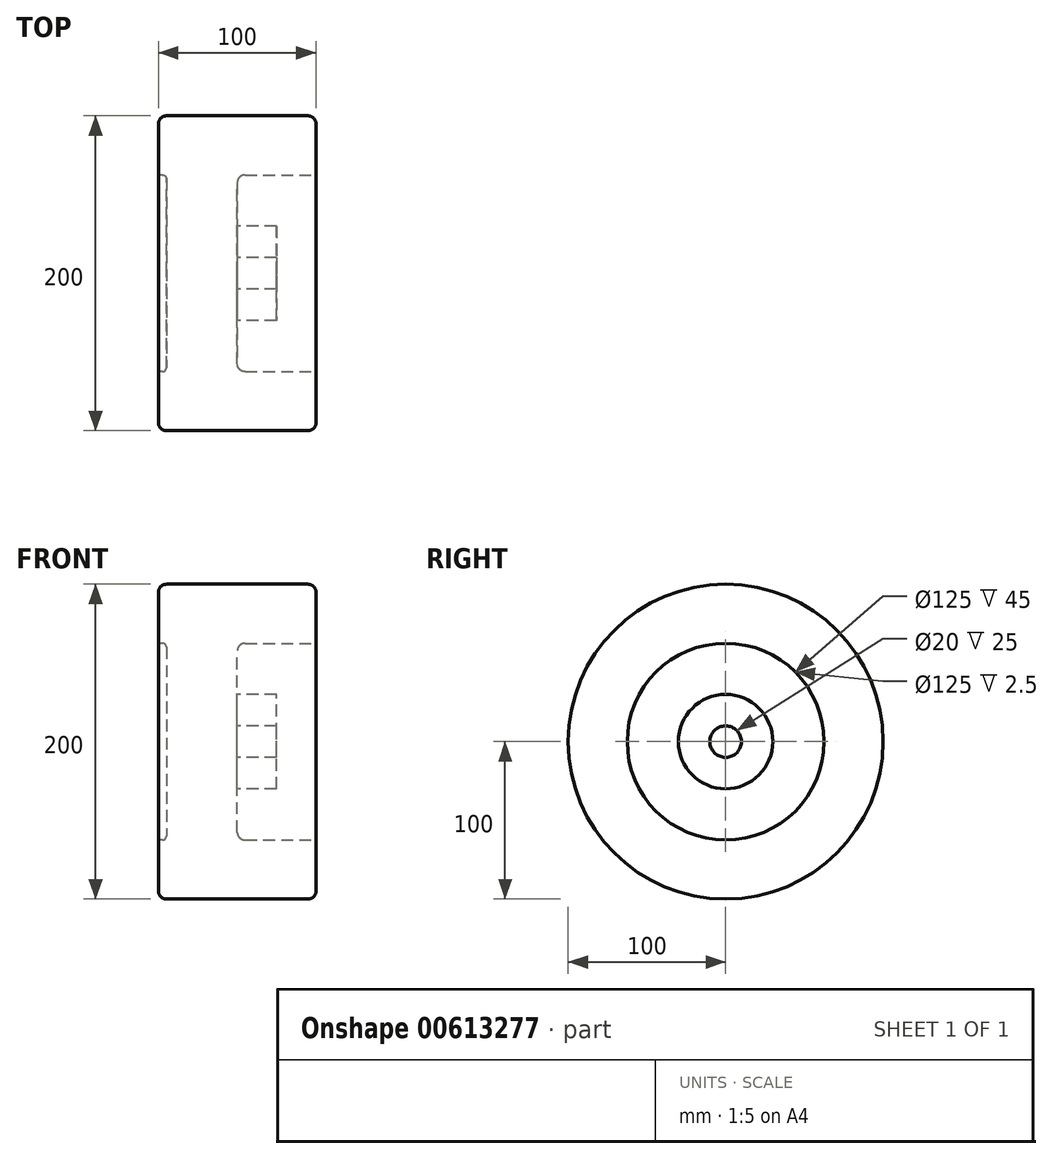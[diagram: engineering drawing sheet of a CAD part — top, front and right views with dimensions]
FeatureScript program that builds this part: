
annotation { "Feature Type Name" : "Feature", "Feature Type Description" : "" }
export const myFeature = defineFeature(function(context is Context, id is Id, definition is map)
    precondition{}
    {
        {
            var Q0;
            Q0=qCreatedBy(makeId("Right.planeOp"),FACE);
            var sketch = newSketch(context, id + "F0", { "sketchPlane" : qUnion([Q0])});
            skCircle(sketch, "E0", {"center": v(0, 0) * mm, "radius": 100 * mm});
            skSolve(sketch);
        }
        {
            var Q0;
            Q0 = qSketchRegion(id + "F0", true);
            extrude(context, id + "F1", {"entities" : qUnion([Q0]), "depth" : 100 * mm, "offsetDistance" : 25 * mm});
        }
        {
            var Q0;
            Q0=makeQuery(id+"F1.opExtrude","CAP_EDGE",EDGE,{"disambiguationData":[OSD([sQuery(id+"F0.wireOp",EDGE,"E0")])],"isStart":false});
            var Q1;
            Q1=makeQuery(id+"F1.opExtrude","CAP_EDGE",EDGE,{"disambiguationData":[OSD([sQuery(id+"F0.wireOp",EDGE,"E0")])],"isStart":true});
            fillet(context, id + "F2", {"entities" : qUnion([Q0, Q1]), "radius" : 5 * mm, "tangentPropagation" : true, "allowEdgeOverflow" : false});
        }
        {
            var Q0;
            Q0=makeQuery(id+"F1.opExtrude","CAP_FACE",FACE,{"disambiguationData":[OSD([sQuery(id+"F0.wireOp",EDGE,"E0")])],"isStart":false});
            var sketch = newSketch(context, id + "F3", { "sketchPlane" : qUnion([Q0])});
            skCircle(sketch, "E1", {"center": v(0, 0) * mm, "radius": 62.5 * mm});
            skSolve(sketch);
        }
        {
            var Q0;
            Q0=makeQuery(id+"F3.imprint","IMPRINT",FACE,{"disambiguationData":[TD([[makeQuery(id+"F3.imprint","IMPRINT",EDGE,{"derivedFrom":sQuery(id+"F3.wireOp",EDGE,"E1")}),1.0]])]});
            extrude(context, id + "F4", {"entities" : qUnion([Q0]), "operationType" : NewBodyOperationType.REMOVE, "oppositeDirection" : true, "depth" : 50 * mm, "offsetDistance" : 25 * mm});
        }
        {
            var Q0;
            Q0=makeQuery(id+"F4.boolean.opBoolean","COPY",FACE,{"derivedFrom":makeQuery(id+"F4.opExtrude","CAP_FACE",FACE,{"disambiguationData":[OSD([sQuery(id+"F3.wireOp",EDGE,"E1")])],"isStart":false})});
            var sketch = newSketch(context, id + "F5", { "sketchPlane" : qUnion([Q0])});
            skCircle(sketch, "E2", {"center": v(0, 0) * mm, "radius": 30 * mm});
            skCircle(sketch, "E3", {"center": v(0, 0) * mm, "radius": 10 * mm});
            skSolve(sketch);
        }
        {
            var Q0;
            Q0=makeQuery(id+"F5.imprint","IMPRINT",FACE,{"disambiguationData":[TD([[makeQuery(id+"F5.imprint","IMPRINT",EDGE,{"derivedFrom":sQuery(id+"F5.wireOp",EDGE,"E2")}),1.0]])]});
            extrude(context, id + "F6", {"entities" : qUnion([Q0]), "operationType" : NewBodyOperationType.ADD, "depth" : 25 * mm, "offsetDistance" : 25 * mm});
        }
        {
            var Q0;
            Q0=makeQuery(id+"F4.boolean.opBoolean","COPY",EDGE,{"derivedFrom":makeQuery(id+"F4.opExtrude","CAP_EDGE",EDGE,{"disambiguationData":[OSD([sQuery(id+"F3.wireOp",EDGE,"E1")])],"isStart":false})});
            var Q1;
            Q1=makeQuery(id+"F4.boolean.opBoolean","COPY",EDGE,{"derivedFrom":makeQuery(id+"F4.opExtrude","CAP_EDGE",EDGE,{"disambiguationData":[OSD([sQuery(id+"F3.wireOp",EDGE,"E1")])],"isStart":true})});
            var Q2;
            Q2=makeQuery(id+"F6.opExtrude","CAP_EDGE",EDGE,{"disambiguationData":[OSD([sQuery(id+"F5.wireOp",EDGE,"E2")])],"isStart":true});
            fillet(context, id + "F7", {"entities" : qUnion([Q0, Q1, Q2]), "radius" : 5 * mm, "tangentPropagation" : true, "allowEdgeOverflow" : false});
        }
        {
            var Q0;
            Q0=makeQuery(id+"F1.opExtrude","CAP_FACE",FACE,{"disambiguationData":[OSD([sQuery(id+"F0.wireOp",EDGE,"E0")])],"isStart":true});
            var sketch = newSketch(context, id + "F8", { "sketchPlane" : qUnion([Q0])});
            skCircle(sketch, "E4", {"center": v(0, 0) * mm, "radius": 62.5 * mm});
            skSolve(sketch);
        }
        {
            var Q0;
            Q0=makeQuery(id+"F8.imprint","IMPRINT",FACE,{"disambiguationData":[TD([[makeQuery(id+"F8.imprint","IMPRINT",EDGE,{"derivedFrom":sQuery(id+"F8.wireOp",EDGE,"E4")}),1.0]])]});
            extrude(context, id + "F9", {"entities" : qUnion([Q0]), "operationType" : NewBodyOperationType.REMOVE, "oppositeDirection" : true, "depth" : 5 * mm, "offsetDistance" : 25 * mm});
        }
        {
            var Q0;
            Q0=makeQuery(id+"F9.boolean.opBoolean","COPY",EDGE,{"derivedFrom":makeQuery(id+"F9.opExtrude","CAP_EDGE",EDGE,{"disambiguationData":[OSD([sQuery(id+"F8.wireOp",EDGE,"E4")])],"isStart":true})});
            var Q1;
            Q1=makeQuery(id+"F9.boolean.opBoolean","COPY",EDGE,{"derivedFrom":makeQuery(id+"F9.opExtrude","CAP_EDGE",EDGE,{"disambiguationData":[OSD([sQuery(id+"F8.wireOp",EDGE,"E4")])],"isStart":false})});
            fillet(context, id + "F10", {"entities" : qUnion([Q0, Q1]), "radius" : 2.5 * mm, "tangentPropagation" : true, "allowEdgeOverflow" : false});
        }
    });
